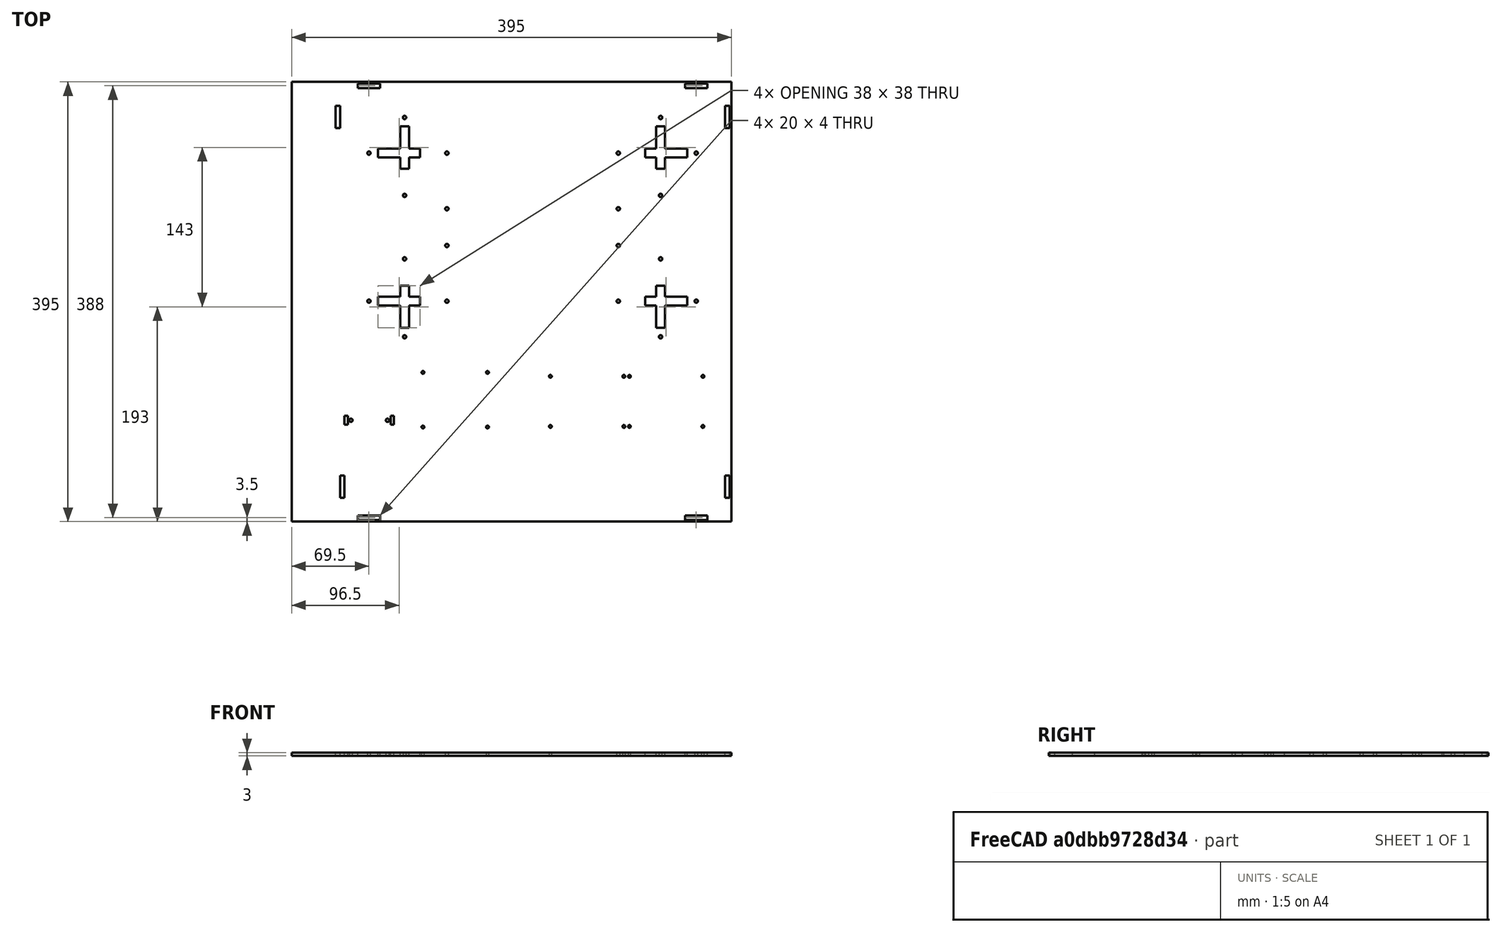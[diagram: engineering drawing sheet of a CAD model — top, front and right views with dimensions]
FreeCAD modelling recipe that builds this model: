
FCSTD DOCUMENT  (FreeCAD 0.19R24366 (Git))
Label: ri_baseplate
License: All rights reserved
LicenseURL: http://en.wikipedia.org/wiki/All_rights_reserved
objects: Sketcher::SketchObject×1, Spreadsheet::Sheet×1, PartDesign::Pad×1, PartDesign::Body×1, App::Part×1
note: 4 computed .brp shape members not serialized (recipe doc carries the construction recipe); baked Part::Feature solids carry a one-line shape summary decoded from their .brp

FEATURE [Sketcher::SketchObject] Sketch
  FullyConstrained = true
  MapMode = 5
  Support = -> [XY_Plane001]
  expr: Constraints[9] = <<Value_Spreadsheet>>.baseplate_size
  expr: Constraints[39] = <<Value_Spreadsheet>>.vert_tab_length
  expr: Constraints[40] = <<Value_Spreadsheet>>.hor_tab_length
  expr: Constraints[122] = <<Value_Spreadsheet>>.vert_tab_length
  expr: Constraints[123] = <<Value_Spreadsheet>>.vert_tab_length
  expr: Constraints[121] = <<Value_Spreadsheet>>.hor_tab_length
  expr: Constraints[124] = <<Value_Spreadsheet>>.vert_tab_length
  expr: Constraints[125] = <<Value_Spreadsheet>>.hor_tab_length
  expr: Constraints[126] = <<Value_Spreadsheet>>.hor_tab_length
  sketch-geometry (136):
    g0: LineSegment StartX=-197.5 StartY=197.5 StartZ=0 EndX=197.5 EndY=197.5 EndZ=0
    g1: LineSegment StartX=197.5 StartY=197.5 StartZ=0 EndX=197.5 EndY=-197.5 EndZ=0
    g2: LineSegment StartX=197.5 StartY=-197.5 StartZ=0 EndX=-197.5 EndY=-197.5 EndZ=0
    g3: LineSegment StartX=-197.5 StartY=-197.5 StartZ=0 EndX=-197.5 EndY=197.5 EndZ=0
    g4: LineSegment StartX=-100 StartY=157.5 StartZ=0 EndX=-92 EndY=157.5 EndZ=0
    g5: LineSegment StartX=-92 StartY=157.5 StartZ=0 EndX=-92 EndY=137.5 EndZ=0
    g6: LineSegment StartX=-92 StartY=119.5 StartZ=0 EndX=-100 EndY=119.5 EndZ=0
    g7: LineSegment StartX=-100 StartY=119.5 StartZ=0 EndX=-100 EndY=129.5 EndZ=0
    g8: LineSegment StartX=-120 StartY=137.5 StartZ=0 EndX=-100 EndY=137.5 EndZ=0
    g9: LineSegment StartX=-82 StartY=137.5 StartZ=0 EndX=-82 EndY=129.5 EndZ=0
    g10: LineSegment StartX=-82 StartY=129.5 StartZ=0 EndX=-92 EndY=129.5 EndZ=0
    g11: LineSegment StartX=-120 StartY=129.5 StartZ=0 EndX=-120 EndY=137.5 EndZ=0
    g12: LineSegment StartX=-100 StartY=137.5 StartZ=0 EndX=-100 EndY=157.5 EndZ=0
    g13: LineSegment StartX=-92 StartY=129.5 StartZ=0 EndX=-92 EndY=119.5 EndZ=0
    g14: LineSegment StartX=-92 StartY=137.5 StartZ=0 EndX=-82 EndY=137.5 EndZ=0
    g15: LineSegment StartX=-100 StartY=129.5 StartZ=0 EndX=-120 EndY=129.5 EndZ=0
    g16: LineSegment StartX=120 StartY=137.5 StartZ=0 EndX=130 EndY=137.5 EndZ=0
    g17: LineSegment StartX=158 StartY=137.5 StartZ=0 EndX=158 EndY=129.5 EndZ=0
    g18: LineSegment StartX=158 StartY=129.5 StartZ=0 EndX=138 EndY=129.5 EndZ=0
    g19: LineSegment StartX=120 StartY=129.5 StartZ=0 EndX=120 EndY=137.5 EndZ=0
    g20: LineSegment StartX=130 StartY=157.5 StartZ=0 EndX=138 EndY=157.5 EndZ=0
    g21: LineSegment StartX=138 StartY=157.5 StartZ=0 EndX=138 EndY=137.5 EndZ=0
    g22: LineSegment StartX=138 StartY=119.5 StartZ=0 EndX=130 EndY=119.5 EndZ=0
    g23: LineSegment StartX=130 StartY=119.5 StartZ=0 EndX=130 EndY=129.5 EndZ=0
    g24: LineSegment StartX=-100 StartY=14.5 StartZ=0 EndX=-92 EndY=14.5 EndZ=0
    g25: LineSegment StartX=-92 StartY=14.5 StartZ=0 EndX=-92 EndY=4.5 EndZ=0
    g26: LineSegment StartX=-92 StartY=-23.5 StartZ=0 EndX=-100 EndY=-23.5 EndZ=0
    g27: LineSegment StartX=-100 StartY=-23.5 StartZ=0 EndX=-100 EndY=-3.5 EndZ=0
    g28: LineSegment StartX=-82 StartY=4.5 StartZ=0 EndX=-92 EndY=4.5 EndZ=0
    g29: LineSegment StartX=-120 StartY=4.5 StartZ=0 EndX=-120 EndY=-3.5 EndZ=0
    g30: LineSegment StartX=-120 StartY=-3.5 StartZ=0 EndX=-100 EndY=-3.5 EndZ=0
    g31: LineSegment StartX=-82 StartY=-3.5 StartZ=0 EndX=-82 EndY=4.5 EndZ=0
    g32: LineSegment StartX=130 StartY=14.5 StartZ=0 EndX=138 EndY=14.5 EndZ=0
    g33: LineSegment StartX=138 StartY=14.5 StartZ=0 EndX=138 EndY=4.5 EndZ=0
    g34: LineSegment StartX=138 StartY=-23.5 StartZ=0 EndX=130 EndY=-23.5 EndZ=0
    g35: LineSegment StartX=130 StartY=-23.5 StartZ=0 EndX=130 EndY=-3.5 EndZ=0
    g36: LineSegment StartX=120 StartY=4.5 StartZ=0 EndX=130 EndY=4.5 EndZ=0
    g37: LineSegment StartX=158 StartY=4.5 StartZ=0 EndX=158 EndY=-3.5 EndZ=0
    g38: LineSegment StartX=158 StartY=-3.5 StartZ=0 EndX=138 EndY=-3.5 EndZ=0
    g39: LineSegment StartX=120 StartY=-3.5 StartZ=0 EndX=120 EndY=4.5 EndZ=0
    g40: LineSegment StartX=138 StartY=137.5 StartZ=0 EndX=158 EndY=137.5 EndZ=0
    g41: LineSegment StartX=130 StartY=137.5 StartZ=0 EndX=130 EndY=157.5 EndZ=0
    g42: LineSegment StartX=130 StartY=129.5 StartZ=0 EndX=120 EndY=129.5 EndZ=0
    g43: LineSegment StartX=138 StartY=129.5 StartZ=0 EndX=138 EndY=119.5 EndZ=0
    g44: LineSegment StartX=138 StartY=4.5 StartZ=0 EndX=158 EndY=4.5 EndZ=0
    g45: LineSegment StartX=130 StartY=4.5 StartZ=0 EndX=130 EndY=14.5 EndZ=0
    g46: LineSegment StartX=130 StartY=-3.5 StartZ=0 EndX=120 EndY=-3.5 EndZ=0
    g47: LineSegment StartX=138 StartY=-3.5 StartZ=0 EndX=138 EndY=-23.5 EndZ=0
    g48: LineSegment StartX=-100 StartY=4.5 StartZ=0 EndX=-120 EndY=4.5 EndZ=0
    g49: LineSegment StartX=-100 StartY=4.5 StartZ=0 EndX=-100 EndY=14.5 EndZ=0
    g50: LineSegment StartX=-92 StartY=-3.5 StartZ=0 EndX=-82 EndY=-3.5 EndZ=0
    g51: LineSegment StartX=-92 StartY=-3.5 StartZ=0 EndX=-92 EndY=-23.5 EndZ=0
    g52: Circle CenterX=-21.5 CenterY=-63.5 CenterZ=0 NormalX=0 NormalY=0 NormalZ=1 AngleXU=0 Radius=1.25
    g53: Circle CenterX=-21.5 CenterY=-112.5 CenterZ=0 NormalX=0 NormalY=0 NormalZ=1 AngleXU=0 Radius=1.25
    g54: GeomPoint X=-82 Y=133.5 Z=0
    g55: GeomPoint X=120 Y=133.5 Z=0
    g56: Circle CenterX=-58 CenterY=133.5 CenterZ=0 NormalX=0 NormalY=0 NormalZ=1 AngleXU=0 Radius=1.5
    g57: Circle CenterX=96 CenterY=133.5 CenterZ=0 NormalX=0 NormalY=0 NormalZ=1 AngleXU=0 Radius=1.5
    g58: Circle CenterX=-58 CenterY=0.5 CenterZ=0 NormalX=0 NormalY=0 NormalZ=1 AngleXU=0 Radius=1.5
    g59: Circle CenterX=96 CenterY=0.5 CenterZ=0 NormalX=0 NormalY=0 NormalZ=1 AngleXU=0 Radius=1.5
    g60: GeomPoint X=19 Y=133.5 Z=0
    g61: GeomPoint X=-82 Y=0.5 Z=0
    g62: GeomPoint X=120 Y=0.5 Z=0
    g63: GeomPoint X=19 Y=0.5 Z=0
    g64: Circle CenterX=-58 CenterY=83.5 CenterZ=0 NormalX=0 NormalY=0 NormalZ=1 AngleXU=0 Radius=1.5
    g65: Circle CenterX=-58 CenterY=50.5 CenterZ=0 NormalX=0 NormalY=0 NormalZ=1 AngleXU=0 Radius=1.5
    g66: Circle CenterX=96 CenterY=83.5 CenterZ=0 NormalX=0 NormalY=0 NormalZ=1 AngleXU=0 Radius=1.5
    g67: Circle CenterX=96 CenterY=50.5 CenterZ=0 NormalX=0 NormalY=0 NormalZ=1 AngleXU=0 Radius=1.5
    g68: Circle CenterX=-128 CenterY=133.5 CenterZ=0 NormalX=0 NormalY=0 NormalZ=1 AngleXU=0 Radius=1.5
    g69: Circle CenterX=-96 CenterY=165.5 CenterZ=0 NormalX=0 NormalY=0 NormalZ=1 AngleXU=0 Radius=1.5
    g70: Circle CenterX=-96 CenterY=95.5 CenterZ=0 NormalX=0 NormalY=0 NormalZ=1 AngleXU=0 Radius=1.5
    g71: Circle CenterX=-96 CenterY=38.5 CenterZ=0 NormalX=0 NormalY=0 NormalZ=1 AngleXU=0 Radius=1.5
    g72: Circle CenterX=-128 CenterY=0.5 CenterZ=0 NormalX=0 NormalY=0 NormalZ=1 AngleXU=0 Radius=1.5
    g73: Circle CenterX=-96 CenterY=-31.5 CenterZ=0 NormalX=0 NormalY=0 NormalZ=1 AngleXU=0 Radius=1.5
    g74: Circle CenterX=134 CenterY=-31.5 CenterZ=0 NormalX=0 NormalY=0 NormalZ=1 AngleXU=0 Radius=1.5
    g75: Circle CenterX=166 CenterY=0.5 CenterZ=0 NormalX=0 NormalY=0 NormalZ=1 AngleXU=0 Radius=1.5
    g76: Circle CenterX=134 CenterY=38.5 CenterZ=0 NormalX=0 NormalY=0 NormalZ=1 AngleXU=0 Radius=1.5
    g77: Circle CenterX=134 CenterY=95.5 CenterZ=0 NormalX=0 NormalY=0 NormalZ=1 AngleXU=0 Radius=1.5
    g78: Circle CenterX=166 CenterY=133.5 CenterZ=0 NormalX=0 NormalY=0 NormalZ=1 AngleXU=0 Radius=1.5
    g79: Circle CenterX=134 CenterY=165.5 CenterZ=0 NormalX=0 NormalY=0 NormalZ=1 AngleXU=0 Radius=1.5
    g80: GeomPoint X=134 Y=119.5 Z=0
    g81: GeomPoint X=-96 Y=119.5 Z=0
    g82: LineSegment StartX=156 StartY=196 StartZ=0 EndX=176 EndY=196 EndZ=0
    g83: LineSegment StartX=176 StartY=196 StartZ=0 EndX=176 EndY=192 EndZ=0
    g84: LineSegment StartX=176 StartY=192 StartZ=0 EndX=156 EndY=192 EndZ=0
    g85: LineSegment StartX=156 StartY=192 StartZ=0 EndX=156 EndY=196 EndZ=0
    g86: LineSegment StartX=192 StartY=176 StartZ=0 EndX=196 EndY=176 EndZ=0
    g87: LineSegment StartX=196 StartY=176 StartZ=0 EndX=196 EndY=156 EndZ=0
    g88: LineSegment StartX=196 StartY=156 StartZ=0 EndX=192 EndY=156 EndZ=0
    g89: LineSegment StartX=192 StartY=156 StartZ=0 EndX=192 EndY=176 EndZ=0
    g90: LineSegment StartX=-138 StartY=196 StartZ=0 EndX=-118 EndY=196 EndZ=0
    g91: LineSegment StartX=-118 StartY=196 StartZ=0 EndX=-118 EndY=192 EndZ=0
    g92: LineSegment StartX=-118 StartY=192 StartZ=0 EndX=-138 EndY=192 EndZ=0
    g93: LineSegment StartX=-138 StartY=192 StartZ=0 EndX=-138 EndY=196 EndZ=0
    g94: LineSegment StartX=-158 StartY=176 StartZ=0 EndX=-154 EndY=176 EndZ=0
    g95: LineSegment StartX=-154 StartY=176 StartZ=0 EndX=-154 EndY=156 EndZ=0
    g96: LineSegment StartX=-154 StartY=156 StartZ=0 EndX=-158 EndY=156 EndZ=0
    g97: LineSegment StartX=-158 StartY=156 StartZ=0 EndX=-158 EndY=176 EndZ=0
    g98: LineSegment StartX=-150 StartY=-156 StartZ=0 EndX=-154 EndY=-156 EndZ=0
    g99: LineSegment StartX=-154 StartY=-156 StartZ=0 EndX=-154 EndY=-176 EndZ=0
    g100: LineSegment StartX=-154 StartY=-176 StartZ=0 EndX=-150 EndY=-176 EndZ=0
    g101: LineSegment StartX=-150 StartY=-176 StartZ=0 EndX=-150 EndY=-156 EndZ=0
    g102: LineSegment StartX=-138 StartY=-192 StartZ=0 EndX=-118 EndY=-192 EndZ=0
    g103: LineSegment StartX=-118 StartY=-192 StartZ=0 EndX=-118 EndY=-196 EndZ=0
    g104: LineSegment StartX=-118 StartY=-196 StartZ=0 EndX=-138 EndY=-196 EndZ=0
    g105: LineSegment StartX=-138 StartY=-196 StartZ=0 EndX=-138 EndY=-192 EndZ=0
    g106: LineSegment StartX=156 StartY=-192 StartZ=0 EndX=176 EndY=-192 EndZ=0
    g107: LineSegment StartX=176 StartY=-192 StartZ=0 EndX=176 EndY=-196 EndZ=0
    g108: LineSegment StartX=176 StartY=-196 StartZ=0 EndX=156 EndY=-196 EndZ=0
    g109: LineSegment StartX=156 StartY=-196 StartZ=0 EndX=156 EndY=-192 EndZ=0
    g110: LineSegment StartX=196 StartY=-156 StartZ=0 EndX=192 EndY=-156 EndZ=0
    g111: LineSegment StartX=192 StartY=-156 StartZ=0 EndX=192 EndY=-176 EndZ=0
    g112: LineSegment StartX=192 StartY=-176 StartZ=0 EndX=196 EndY=-176 EndZ=0
    g113: LineSegment StartX=196 StartY=-176 StartZ=0 EndX=196 EndY=-156 EndZ=0
    g114: Circle CenterX=35 CenterY=-67 CenterZ=0 NormalX=0 NormalY=0 NormalZ=1 AngleXU=0 Radius=1.25
    g115: Circle CenterX=35 CenterY=-112 CenterZ=0 NormalX=0 NormalY=0 NormalZ=1 AngleXU=0 Radius=1.25
    g116: Circle CenterX=101 CenterY=-67 CenterZ=0 NormalX=0 NormalY=0 NormalZ=1 AngleXU=0 Radius=1.25
    g117: Circle CenterX=106 CenterY=-67 CenterZ=0 NormalX=0 NormalY=0 NormalZ=1 AngleXU=0 Radius=1.25
    g118: Circle CenterX=172 CenterY=-67 CenterZ=0 NormalX=0 NormalY=0 NormalZ=1 AngleXU=0 Radius=1.25
    g119: Circle CenterX=172 CenterY=-112 CenterZ=0 NormalX=0 NormalY=0 NormalZ=1 AngleXU=0 Radius=1.25
    g120: Circle CenterX=106 CenterY=-112 CenterZ=0 NormalX=0 NormalY=0 NormalZ=1 AngleXU=0 Radius=1.25
    g121: Circle CenterX=101 CenterY=-112 CenterZ=0 NormalX=0 NormalY=0 NormalZ=1 AngleXU=0 Radius=1.25
    g122: Circle CenterX=-79.5 CenterY=-63.5 CenterZ=0 NormalX=0 NormalY=0 NormalZ=1 AngleXU=0 Radius=1.25
    g123: Circle CenterX=-79.5 CenterY=-112.5 CenterZ=0 NormalX=0 NormalY=0 NormalZ=1 AngleXU=0 Radius=1.25
    g124: LineSegment StartX=-108.5 StartY=-110.5 StartZ=0 EndX=-105.5 EndY=-110.5 EndZ=0
    g125: LineSegment StartX=-105.5 StartY=-110.5 StartZ=0 EndX=-105.5 EndY=-102.5 EndZ=0
    g126: LineSegment StartX=-105.5 StartY=-102.5 StartZ=0 EndX=-108.5 EndY=-102.5 EndZ=0
    g127: LineSegment StartX=-108.5 StartY=-102.5 StartZ=0 EndX=-108.5 EndY=-110.5 EndZ=0
    g128: LineSegment StartX=-150 StartY=-102.5 StartZ=0 EndX=-147 EndY=-102.5 EndZ=0
    g129: LineSegment StartX=-147 StartY=-102.5 StartZ=0 EndX=-147 EndY=-110.5 EndZ=0
    g130: LineSegment StartX=-147 StartY=-110.5 StartZ=0 EndX=-150 EndY=-110.5 EndZ=0
    g131: LineSegment StartX=-150 StartY=-110.5 StartZ=0 EndX=-150 EndY=-102.5 EndZ=0
    g132: GeomPoint X=19 Y=-196 Z=0
    g133: Circle CenterX=-144.2 CenterY=-106.5 CenterZ=0 NormalX=0 NormalY=0 NormalZ=1 AngleXU=0 Radius=1.5
    g134: Circle CenterX=-111.3 CenterY=-106.5 CenterZ=0 NormalX=0 NormalY=0 NormalZ=1 AngleXU=0 Radius=1.5
    g135: LineSegment StartX=-150 StartY=-106.5 StartZ=0 EndX=-105.5 EndY=-106.5 EndZ=0
  constraints (361):
    c: Coincident(g0,g1)
    c: Coincident(g1,g2)
    c: Coincident(g2,g3)
    c: Coincident(g3,g0)
    c: Horizontal(g0)
    c: Horizontal(g2)
    c: Vertical(g1)
    c: Vertical(g3)
    c: Equal(g0,g3)
    c: DistanceX(g0,g0) = 395
    c: Symmetric(g0,g1,g-1)
    c: Coincident(g4,g5)
    c: Coincident(g13,g6)
    c: Coincident(g6,g7)
    c: Coincident(g12,g4)
    c: Horizontal(g4)
    c: Horizontal(g6)
    c: Vertical(g5)
    c: Vertical(g7)
    c: Coincident(g14,g9)
    c: Coincident(g9,g10)
    c: Coincident(g15,g11)
    c: Coincident(g11,g8)
    c: Horizontal(g8)
    c: Horizontal(g10)
    c: Vertical(g9)
    c: Vertical(g11)
    c: Tangent(g7,g12)
    c: Tangent(g5,g13)
    c: Coincident(g8,g12)
    c: Coincident(g14,g5)
    c: Tangent(g8,g14)
    c: Coincident(g10,g13)
    c: Coincident(g15,g7)
    c: Tangent(g10,g15)
    c: Equal(g13,g10)
    c: DistanceX(g10,g10) = 10
    c: Equal(g6,g9)
    c: DistanceY(g11,g11) = 8
    c: DistanceY(g6,g4) = 38
    c: DistanceX(g11,g9) = 38
    c: Coincident(g40,g17)
    c: Coincident(g17,g18)
    c: Coincident(g42,g19)
    c: Coincident(g19,g16)
    c: Horizontal(g16)
    c: Horizontal(g18)
    c: Vertical(g17)
    c: Vertical(g19)
    c: Coincident(g20,g21)
    c: Coincident(g43,g22)
    c: Coincident(g22,g23)
    c: Coincident(g41,g20)
    c: Vertical(g21)
    c: Vertical(g23)
    c: Coincident(g24,g25)
    c: Coincident(g51,g26)
    c: Coincident(g26,g27)
    c: Coincident(g49,g24)
    c: Horizontal(g24)
    c: Horizontal(g26)
    c: Vertical(g25)
    c: Vertical(g27)
    c: Coincident(g48,g29)
    c: Coincident(g29,g30)
    c: Coincident(g50,g31)
    c: Coincident(g31,g28)
    c: Horizontal(g28)
    c: Horizontal(g30)
    c: Coincident(g32,g33)
    c: Coincident(g47,g34)
    c: Coincident(g34,g35)
    c: Coincident(g45,g32)
    c: Vertical(g33)
    c: Vertical(g35)
    c: Coincident(g44,g37)
    c: Coincident(g37,g38)
    c: Coincident(g46,g39)
    c: Coincident(g39,g36)
    c: Horizontal(g36)
    c: Horizontal(g38)
    c: Tangent(g16,g40)
    c: Coincident(g41,g16)
    c: Tangent(g23,g41)
    c: Coincident(g42,g23)
    c: Tangent(g18,g42)
    c: Coincident(g21,g40)
    c: Coincident(g43,g18)
    c: Tangent(g21,g43)
    c: Tangent(g36,g44)
    c: Coincident(g45,g36)
    c: Tangent(g35,g45)
    c: Coincident(g46,g35)
    c: Tangent(g38,g46)
    c: Coincident(g33,g44)
    c: Coincident(g47,g38)
    c: Tangent(g33,g47)
    c: Tangent(g28,g48)
    c: Coincident(g49,g48)
    c: Tangent(g27,g49)
    c: Coincident(g30,g27)
    c: Tangent(g30,g50)
    c: Coincident(g25,g28)
    c: Coincident(g51,g50)
    c: Tangent(g25,g51)
    c: Equal(g13,g25)
    c: Equal(g28,g25)
    c: Equal(g45,g36)
    c: Equal(g45,g10)
    c: Equal(g42,g23)
    c: Equal(g42,g10)
    c: Equal(g9,g19)
    c: Equal(g19,g22)
    c: Equal(g32,g39)
    c: Equal(g22,g32)
    c: Equal(g31,g24)
    c: Equal(g24,g6)
    c: Tangent(g9,g31)
    c: Tangent(g6,g22)
    c: Tangent(g39,g19)
    c: Tangent(g24,g32)
    c: DistanceX(g19,g17) = 38
    c: DistanceY(g22,g20) = 38
    c: DistanceY(g34,g32) = 38
    c: DistanceY(g26,g24) = 38
    c: DistanceX(g29,g28) = 38
    c: DistanceX(g36,g37) = 38
    c: DistanceX(g9,g19) = 202
    c: Vertical(g37)
    c: DistanceY(g24,g6) = 105
    c: Horizontal(g20)
    c: Horizontal(g34)
    c: DistanceX(g0,g17) = -39.5
    c: Vertical(g29)
    c: DistanceY(g20,g0) = 40
    c: DistanceY(g53,g52) = 49
    c: Symmetric(g9,g9,g54)
    c: Symmetric(g16,g19,g55)
    c: Equal(g56,g57)
    c: Equal(g57,g58)
    c: Equal(g58,g59)
    c: DistanceY(g56,g57) = 0
    c: Symmetric(g55,g54,g60)
    c: Symmetric(g56,g57,g60)
    c: DistanceX(g9,g56) = 24
    c: Symmetric(g28,g31,g61)
    c: Symmetric(g36,g39,g62)
    c: Symmetric(g62,g61,g63)
    c: Symmetric(g58,g59,g63)
    c: DistanceY(g59,g58) = 0
    c: DistanceX(g58,g56) = 0
    c: Diameter(g64) = 3
    c: Equal(g65,g64)
    c: Equal(g67,g64)
    c: Equal(g66,g64)
    c: DistanceX(g64,g56) = 0
    c: DistanceX(g65,g64) = 0
    c: DistanceY(g64,g56) = 50
    c: DistanceY(g58,g65) = 50
    c: DistanceY(g67,g65) = 0
    c: DistanceY(g64,g66) = 0
    c: DistanceX(g67,g59) = 0
    c: DistanceX(g66,g67) = 0
    c: Equal(g64,g56)
    c: Symmetric(g22,g22,g80)
    c: Vertical(g77,g80)
    c: Vertical(g79,g80)
    c: Horizontal(g78,g57)
    c: Horizontal(g75,g59)
    c: Vertical(g80,g76)
    c: Vertical(g74,g76)
    c: Horizontal(g72,g58)
    c: Horizontal(g68,g56)
    c: Symmetric(g6,g6,g81)
    c: Vertical(g69,g81)
    c: Vertical(g81,g70)
    c: Vertical(g71,g81)
    c: Equal(g73,g72)
    c: Equal(g72,g71)
    c: Equal(g71,g70)
    c: Equal(g70,g68)
    c: Equal(g68,g69)
    c: Equal(g69,g56)
    c: Equal(g79,g57)
    c: Equal(g57,g78)
    c: Equal(g78,g77)
    c: Equal(g74,g75)
    c: Equal(g75,g76)
    c: Equal(g76,g56)
    c: DistanceX(g37,g75) = 8
    c: DistanceY(g74,g34) = 8
    c: DistanceY(g32,g76) = 24
    c: DistanceY(g77,g22) = 24
    c: DistanceX(g17,g78) = 8
    c: DistanceY(g20,g79) = 8
    c: DistanceY(g4,g69) = 8
    c: DistanceX(g68,g8) = 8
    c: DistanceY(g70,g6) = 24
    c: DistanceY(g24,g71) = 24
    c: DistanceX(g72,g29) = 8
    c: DistanceY(g73,g26) = 8
    c: Vertical(g73,g71)
    c: Coincident(g82,g83)
    c: Coincident(g83,g84)
    c: Coincident(g84,g85)
    c: Coincident(g85,g82)
    c: Horizontal(g82)
    c: Horizontal(g84)
    c: Vertical(g83)
    c: Vertical(g85)
    c: DistanceY(g85,g85) = 4
    c: DistanceX(g82,g82) = 20
    c: Coincident(g86,g87)
    c: Coincident(g87,g88)
    c: Coincident(g88,g89)
    c: Coincident(g89,g86)
    c: Horizontal(g86)
    c: Horizontal(g88)
    c: Vertical(g87)
    c: Vertical(g89)
    c: Equal(g86,g83)
    c: Equal(g89,g84)
    c: DistanceY(g82,g0) = 1.5
    c: DistanceX(g82,g0) = 21.5
    c: DistanceY(g86,g0) = 21.5
    c: DistanceX(g86,g0) = 1.5
    c: Coincident(g90,g91)
    c: Coincident(g91,g92)
    c: Coincident(g92,g93)
    c: Coincident(g93,g90)
    c: Horizontal(g90)
    c: Horizontal(g92)
    c: Vertical(g91)
    c: Vertical(g93)
    c: Coincident(g94,g95)
    c: Coincident(g95,g96)
    c: Coincident(g96,g97)
    c: Coincident(g97,g94)
    c: Horizontal(g94)
    c: Horizontal(g96)
    c: Vertical(g95)
    c: Vertical(g97)
    c: Equal(g91,g85)
    c: Equal(g92,g84)
    c: Equal(g92,g95)
    c: Equal(g93,g94)
    c: Horizontal(g90,g82)
    c: Horizontal(g94,g86)
    c: DistanceX(g96,g8) = 38
    c: DistanceX(g94,g92) = 20
    c: Coincident(g98,g99)
    c: Coincident(g99,g100)
    c: Coincident(g100,g101)
    c: Coincident(g101,g98)
    c: Horizontal(g98)
    c: Horizontal(g100)
    c: Vertical(g99)
    c: Vertical(g101)
    c: Coincident(g102,g103)
    c: Coincident(g103,g104)
    c: Coincident(g104,g105)
    c: Coincident(g105,g102)
    c: Horizontal(g102)
    c: Horizontal(g104)
    c: Vertical(g103)
    c: Vertical(g105)
    c: Coincident(g106,g107)
    c: Coincident(g107,g108)
    c: Coincident(g108,g109)
    c: Coincident(g109,g106)
    c: Horizontal(g106)
    c: Horizontal(g108)
    c: Vertical(g107)
    c: Vertical(g109)
    c: Coincident(g110,g111)
    c: Coincident(g111,g112)
    c: Coincident(g112,g113)
    c: Coincident(g113,g110)
    c: Horizontal(g110)
    c: Horizontal(g112)
    c: Vertical(g111)
    c: Vertical(g113)
    c: Equal(g101,g104)
    c: Equal(g104,g108)
    c: Equal(g108,g111)
    c: Equal(g111,g87)
    c: Equal(g88,g112)
    c: Equal(g112,g107)
    c: Equal(g107,g103)
    c: Equal(g103,g100)
    c: DistanceY(g1,g112) = 21.5
    c: Vertical(g107,g83)
    c: DistanceY(g1,g107) = 1.5
    c: Vertical(g110,g87)
    c: Horizontal(g103,g108)
    c: Horizontal(g99,g111)
    c: Vertical(g95,g98)
    c: Vertical(g102,g92)
    c: Horizontal(g114,g116)
    c: Horizontal(g116,g117)
    c: Horizontal(g117,g118)
    c: Vertical(g115,g114)
    c: Horizontal(g115,g121)
    c: Horizontal(g121,g120)
    c: Horizontal(g120,g119)
    c: Equal(g114, g115-g121) x7
    c: Vertical(g116,g121)
    c: Vertical(g118,g119)
    c: DistanceY(g115,g114) = 45
    c: DistanceX(g114,g116) = 66
    c: Diameter(g114) = 2.5
    c: Vertical(g117,g120)
    c: DistanceX(g117,g118) = 66
    c: DistanceY(g106,g119) = 80
    c: DistanceX(g119,g110) = 20
    c: DistanceX(g116,g117) = 5
    c: Equal(g52,g53)
    c: Equal(g52,g114)
    c: Vertical(g53,g52)
    c: Equal(g122,g123)
    c: Equal(g123,g52)
    c: Vertical(g122,g123)
    c: Horizontal(g122,g52)
    c: Horizontal(g123,g53)
    c: DistanceX(g122,g52) = 58
    c: Coincident(g124,g125)
    c: Coincident(g125,g126)
    c: Coincident(g126,g127)
    c: Coincident(g127,g124)
    c: Horizontal(g124)
    c: Horizontal(g126)
    c: Vertical(g125)
    c: Vertical(g127)
    c: Coincident(g128,g129)
    c: Coincident(g129,g130)
    c: Coincident(g130,g131)
    c: Coincident(g131,g128)
    c: Horizontal(g128)
    c: Horizontal(g130)
    c: Vertical(g129)
    c: Vertical(g131)
    c: Equal(g131,g127)
    c: Equal(g128,g124)
    c: DistanceX(g130,g130) = 3
    c: DistanceY(g131,g131) = 8
    c: DistanceX(g125,g123) = 26
    c: DistanceY(g123,g124) = 2
    c: Horizontal(g129,g124)
    c: DistanceX(g129,g124) = 38.5
    c: Vertical(g130,g98)
    c: DistanceY(g122,g31) = 60
    c: Symmetric(g103,g108,g132)
    c: Equal(g133,g134)
    c: Diameter(g133) = 3
    c: PointOnObject(g135,g131)
    c: PointOnObject(g135,g125)
    c: Symmetric(g126,g124,g135)
    c: PointOnObject(g134,g135)
    c: PointOnObject(g133,g135)
    c: DistanceX(g129,g133) = 2.8
    c: DistanceX(g134,g126) = 2.8
FEATURE [Spreadsheet::Sheet] Spreadsheet  label="Value_Spreadsheet"
  cells = A2=Baseplate Width; B2(baseplate_size)=395; A5=Horizontal Tab; B5(hor_tab_length)=38; A6=Vertical Tab; B6(vert_tab_length)=38
FEATURE [PartDesign::Pad] Pad
  Direction = (1,1,1)
  Length = 3
  Length2 = 100
  Profile = -> Sketch
  Refine = true
  Type = 0
FEATURE [PartDesign::Body] Body
  Group = -> [Sketch,Pad]
  Origin = -> Origin001
  Placement = pos=(200,-200,0) rot=(0,0,1;0rad)
  Tip = -> Pad
FEATURE [App::Part] Part
  Group = -> [Body]
  Origin = -> Origin
